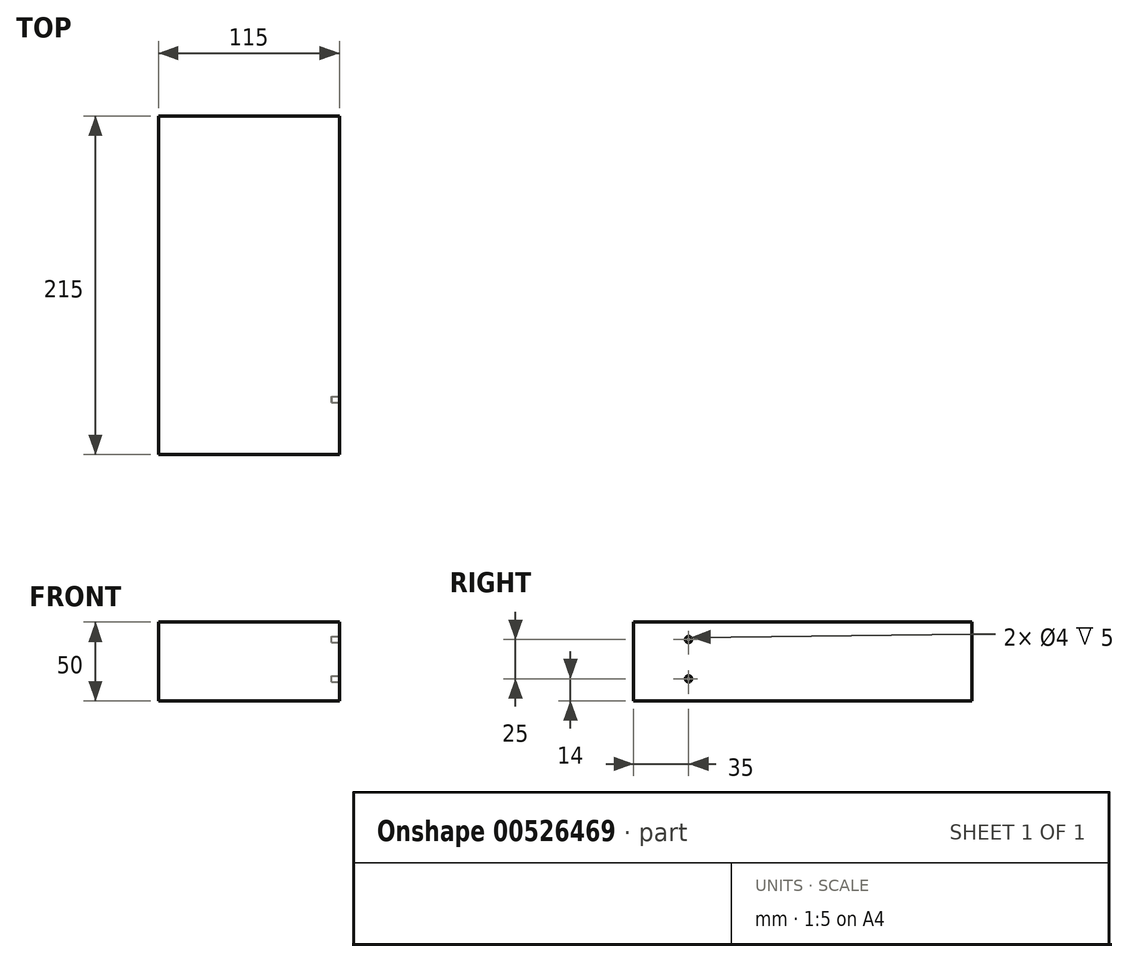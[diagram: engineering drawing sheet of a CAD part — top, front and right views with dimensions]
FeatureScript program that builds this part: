
annotation { "Feature Type Name" : "Feature", "Feature Type Description" : "" }
export const myFeature = defineFeature(function(context is Context, id is Id, definition is map)
    precondition{}
    {
        {
            var Q0;
            Q0=qCreatedBy(makeId("Top.planeOp"),FACE);
            var sketch = newSketch(context, id + "F0", { "sketchPlane" : qUnion([Q0])});
            skLineSegment(sketch, "E0.bottom", {"start": v(57.5, -107.5) * mm, "end": v(-57.5, -107.5) * mm});
            skLineSegment(sketch, "E0.top", {"start": v(57.5, 107.5) * mm, "end": v(-57.5, 107.5) * mm});
            skLineSegment(sketch, "E0.left", {"start": v(57.5, -107.5) * mm, "end": v(57.5, 107.5) * mm});
            skLineSegment(sketch, "E0.right", {"start": v(-57.5, -107.5) * mm, "end": v(-57.5, 107.5) * mm});
            skPoint(sketch, "E0.middle", {"position": v(0, 0) * mm});
            skSolve(sketch);
        }
        {
            var Q0;
            Q0 = qSketchRegion(id + "F0", true);
            extrude(context, id + "F1", {"entities" : qUnion([Q0]), "depth" : 50 * mm, "offsetDistance" : 25 * mm});
        }
        {
            var Q0;
            Q0=makeQuery(id+"F1.opExtrude","SWEPT_FACE",FACE,{"disambiguationData":[OSD([sQuery(id+"F0.wireOp",EDGE,"E0.left")])]});
            var sketch = newSketch(context, id + "F2", { "sketchPlane" : qUnion([Q0])});
            skCircle(sketch, "E1", {"center": v(-72.5, 39) * mm, "radius": 2 * mm});
            skCircle(sketch, "E2", {"center": v(-72.5, 14) * mm, "radius": 2 * mm});
            skSolve(sketch);
        }
        {
            var Q0;
            Q0=makeQuery(id+"F2.imprint","IMPRINT",FACE,{"disambiguationData":[TD([[makeQuery(id+"F2.imprint","IMPRINT",EDGE,{"derivedFrom":sQuery(id+"F2.wireOp",EDGE,"E1")}),1.0]])]});
            var Q1;
            Q1=makeQuery(id+"F2.imprint","IMPRINT",FACE,{"disambiguationData":[TD([[makeQuery(id+"F2.imprint","IMPRINT",EDGE,{"derivedFrom":sQuery(id+"F2.wireOp",EDGE,"E2")}),1.0]])]});
            extrude(context, id + "F3", {"entities" : qUnion([Q0, Q1]), "operationType" : NewBodyOperationType.REMOVE, "oppositeDirection" : true, "depth" : 5 * mm, "offsetDistance" : 25 * mm});
        }
    });
